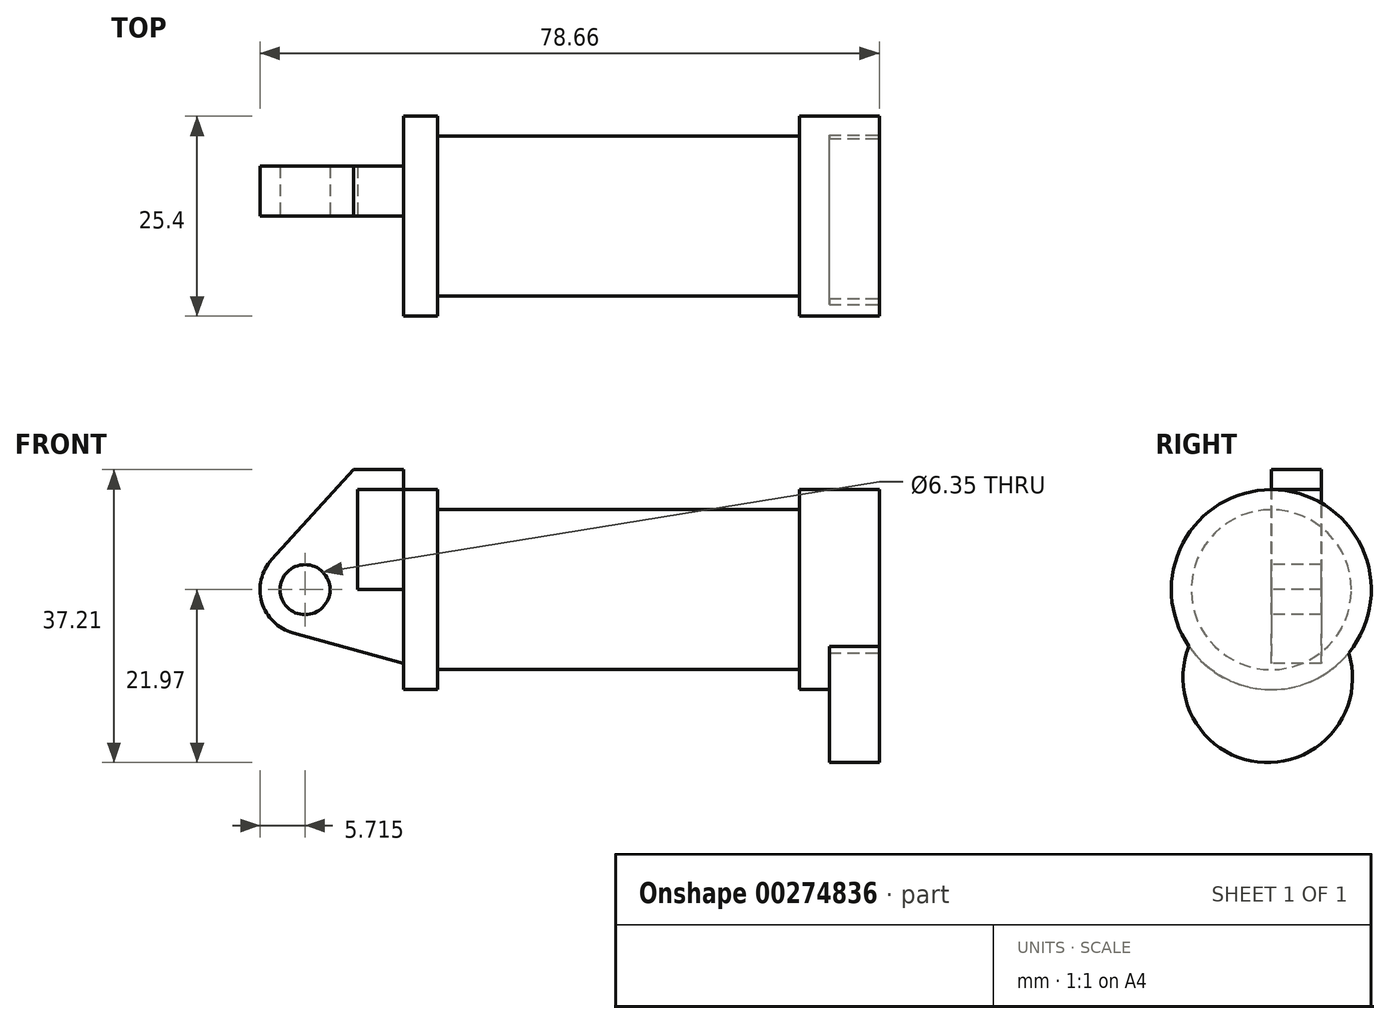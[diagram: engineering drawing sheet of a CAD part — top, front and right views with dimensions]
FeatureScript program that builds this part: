
annotation { "Feature Type Name" : "Feature", "Feature Type Description" : "" }
export const myFeature = defineFeature(function(context is Context, id is Id, definition is map)
    precondition{}
    {
        {
            var Q0;
            Q0=qCreatedBy(makeId("Front.planeOp"),FACE);
            var sketch = newSketch(context, id + "F0", { "sketchPlane" : qUnion([Q0])});
            skLineSegment(sketch, "E0", {"start": v(0, 0) * mm, "end": v(0, 12.7) * mm});
            skLineSegment(sketch, "E1", {"start": v(0, 12.7) * mm, "end": v(10.16, 12.7) * mm});
            skLineSegment(sketch, "E2", {"start": v(10.16, 12.7) * mm, "end": v(10.16, 10.16) * mm});
            skLineSegment(sketch, "E3", {"start": v(10.16, 10.16) * mm, "end": v(56.13, 10.16) * mm});
            skLineSegment(sketch, "E4", {"start": v(56.13, 10.16) * mm, "end": v(56.13, 12.7) * mm});
            skLineSegment(sketch, "E5", {"start": v(56.13, 12.7) * mm, "end": v(66.3, 12.7) * mm});
            skLineSegment(sketch, "E6", {"start": v(66.3, 12.7) * mm, "end": v(66.3, 0) * mm});
            skLineSegment(sketch, "E7", {"start": v(66.3, 0) * mm, "end": v(0, 0) * mm});
            skLineSegment(sketch, "E8", {"start": v(5.84, 15.24) * mm, "end": v(-0.5, 15.24) * mm});
            skLineSegment(sketch, "E9", {"start": v(-0.5, 15.24) * mm, "end": v(-10.88, 3.85) * mm});
            skLineSegment(sketch, "E10", {"start": v(0, 0) * mm, "end": v(-6.65, 0) * mm});
            skCircle(sketch, "E11", {"center": v(-6.65, 0) * mm, "radius": 5.72 * mm});
            skCircle(sketch, "E12", {"center": v(-6.65, 0) * mm, "radius": 3.18 * mm});
            skLineSegment(sketch, "E13", {"start": v(5.84, 15.24) * mm, "end": v(5.84, -9.4) * mm});
            skLineSegment(sketch, "E14", {"start": v(5.84, -9.4) * mm, "end": v(-8.18, -5.5) * mm});
            skSolve(sketch);
        }
        {
            var Q0;
            {var subQ3=sQuery(id+"F0.wireOp",EDGE,"E0");Q0=makeQuery(id+"F0.imprint","IMPRINT",FACE,{"disambiguationData":[TD([[makeQuery(id+"F0.imprint","IMPRINT",EDGE,{"derivedFrom":subQ3}),1.0]])]});}
            var Q1;
            {var subQ4=sQuery(id+"F0.wireOp",EDGE,"E12");Q1=makeQuery(id+"F0.imprint","IMPRINT",FACE,{"disambiguationData":[TD([[makeQuery(id+"F0.imprint","IMPRINT",EDGE,{"derivedFrom":subQ4}),-1.0]])]});}
            var Q2;
            {var subQ0=sQuery(id+"F0.wireOp",EDGE,"E14");Q2=makeQuery(id+"F0.imprint","IMPRINT",FACE,{"disambiguationData":[TD([[makeQuery(id+"F0.imprint","IMPRINT",EDGE,{"derivedFrom":subQ0}),-1.0]])]});}
            extrude(context, id + "F1", {"entities" : qUnion([Q0, Q1, Q2]), "oppositeDirection" : true, "depth" : 6.35 * mm});
        }
        {
            var Q0;
            Q0=sQuery(id+"F0.wireOp",VERTEX,"E10.end");
            var Q1;
            Q1=makeQuery(id+"F1.opExtrude","SWEPT_BODY",BODY,{"disambiguationData":[OSD([sQuery(id+"F0.wireOp",EDGE,"E1"),sQuery(id+"F0.wireOp",EDGE,"E2"),sQuery(id+"F0.wireOp",EDGE,"E3"),sQuery(id+"F0.wireOp",EDGE,"E4"),sQuery(id+"F0.wireOp",EDGE,"E5"),sQuery(id+"F0.wireOp",EDGE,"E6"),sQuery(id+"F0.wireOp",EDGE,"E7"),sQuery(id+"F0.wireOp",EDGE,"E8"),sQuery(id+"F0.wireOp",EDGE,"E9"),sQuery(id+"F0.wireOp",EDGE,"E11"),sQuery(id+"F0.wireOp",EDGE,"E13"),sQuery(id+"F0.wireOp",EDGE,"E14")])]});
            hole(context, id + "F2", {"style" : HoleStyle.SIMPLE, "endStyle" : HoleEndStyle.THROUGH, "oppositeDirection" : true, "holeDiameter" : 6.35 * mm, "tappedDepth" : 12.7 * mm, "tapClearance" : 3, "locations" : qUnion([Q0]), "scope" : qUnion([Q1])});
        }
        {
            var Q0;
            {var subQ0=sQuery(id+"F0.wireOp",EDGE,"E2");Q0=makeQuery(id+"F0.imprint","IMPRINT",FACE,{"disambiguationData":[TD([[makeQuery(id+"F0.imprint","IMPRINT",EDGE,{"derivedFrom":subQ0}),-1.0]])]});}
            var Q1;
            Q1=makeQuery(id+"F1.opExtrude","CAP_EDGE",EDGE,{"disambiguationData":[OSD([sQuery(id+"F0.wireOp",EDGE,"E6")])],"isStart":false});
            var Q2;
            Q2=sQuery(id+"F0.wireOp",EDGE,"E6");
            var Q3;
            Q3=makeQuery(id+"F1.opExtrude","SWEPT_EDGE",EDGE,{"disambiguationData":[OSD([sQuery(id+"F0.wireOp",EDGE,"E6"),sQuery(id+"F0.wireOp",EDGE,"E7")])]});
            var Q4;
            Q4=makeQuery(id+"F1.opExtrude","SWEPT_EDGE",EDGE,{"disambiguationData":[OSD([sQuery(id+"F0.wireOp",EDGE,"E5"),sQuery(id+"F0.wireOp",EDGE,"E6")])]});
            var Q5;
            Q5=sQuery(id+"F0.wireOp",EDGE,"E7");
            revolve(context, id + "F3", {"entities" : qUnion([Q0]), "surfaceEntities" : qUnion([Q1, Q2, Q3, Q4]), "axis" : qUnion([Q5]), "revolveType" : RevolveType.FULL, "oppositeDirection" : true});
        }
        {
            var Q0;
            Q0=makeQuery(id+"F3.opRevolve","SWEPT_FACE",FACE,{"disambiguationData":[OSD([sQuery(id+"F0.wireOp",EDGE,"E6")])]});
            var sketch = newSketch(context, id + "F4", { "sketchPlane" : qUnion([Q0])});
            skLineSegment(sketch, "E15", {"start": v(-10.46, -7.2) * mm, "end": v(-9.84, 8.03) * mm});
            skLineSegment(sketch, "E16", {"start": v(-9.84, 8.03) * mm, "end": v(10.46, 7.2) * mm});
            skLineSegment(sketch, "E17", {"start": v(10.46, 7.2) * mm, "end": v(9.84, -8.03) * mm});
            skArc(sketch, "E18", {"start": v(-10.46, -7.2) * mm, "mid": v(-0.9, -21.96) * mm, "end": v(9.84, -8.03) * mm});
            skSolve(sketch);
        }
        {
            var Q0;
            {var subQ0=sQuery(id+"F4.wireOp",EDGE,"E18");Q0=makeQuery(id+"F4.imprint","IMPRINT",FACE,{"disambiguationData":[TD([[makeQuery(id+"F4.imprint","IMPRINT",EDGE,{"derivedFrom":subQ0}),1.0]])]});}
            var Q1;
            {var subQ0=sQuery(id+"F4.wireOp",EDGE,"E15");Q1=makeQuery(id+"F4.imprint","IMPRINT",FACE,{"disambiguationData":[TD([[makeQuery(id+"F4.imprint","IMPRINT",EDGE,{"derivedFrom":subQ0}),-1.0]])]});}
            extrude(context, id + "F5", {"entities" : qUnion([Q0, Q1]), "operationType" : NewBodyOperationType.ADD, "oppositeDirection" : true, "depth" : 6.35 * mm});
        }
    });
